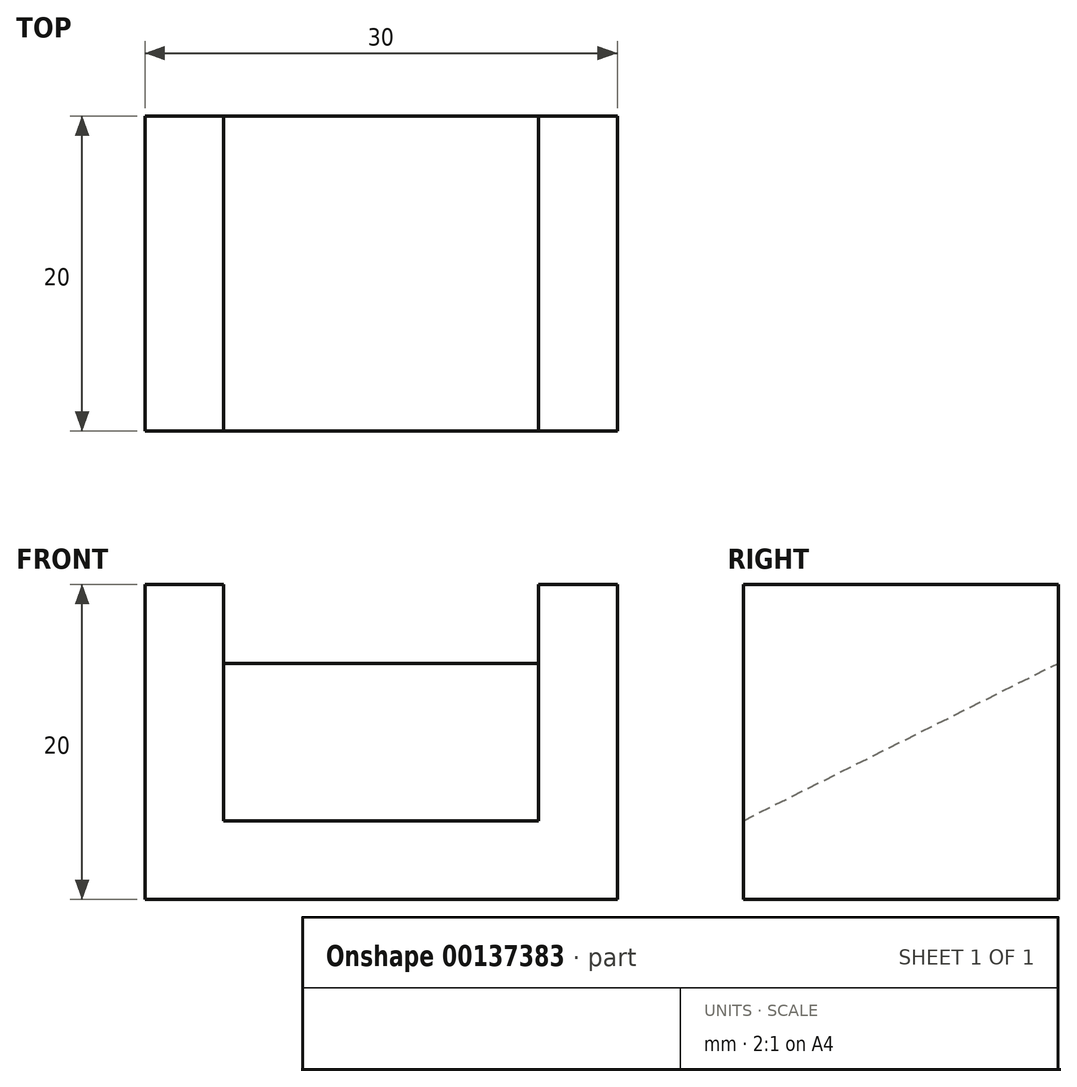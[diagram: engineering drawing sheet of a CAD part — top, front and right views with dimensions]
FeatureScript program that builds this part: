
annotation { "Feature Type Name" : "Feature", "Feature Type Description" : "" }
export const myFeature = defineFeature(function(context is Context, id is Id, definition is map)
    precondition{}
    {
        {
            var Q0;
            Q0=qCreatedBy(makeId("Front.planeOp"),FACE);
            var sketch = newSketch(context, id + "F0", { "sketchPlane" : qUnion([Q0])});
            skLineSegment(sketch, "E0.bottom", {"start": v(-15, 0) * mm, "end": v(15, 0) * mm});
            skLineSegment(sketch, "E0.top", {"start": v(-15, 20) * mm, "end": v(15, 20) * mm});
            skLineSegment(sketch, "E0.left", {"start": v(-15, 0) * mm, "end": v(-15, 20) * mm});
            skLineSegment(sketch, "E0.right", {"start": v(15, 0) * mm, "end": v(15, 20) * mm});
            skSolve(sketch);
        }
        {
            var Q0;
            Q0=qSketchRegion(id+"F0",true);
            extrude(context, id + "F1", {"entities" : qUnion([Q0]), "endBound" : BoundingType.SYMMETRIC, "depth" : 20 * mm});
        }
        {
            var Q0;
            Q0=qCreatedBy(makeId("Right.planeOp"),FACE);
            var sketch = newSketch(context, id + "F2", { "sketchPlane" : qUnion([Q0])});
            skLineSegment(sketch, "E1", {"start": v(10, 15) * mm, "end": v(10, 20) * mm});
            skLineSegment(sketch, "E2", {"start": v(10, 20) * mm, "end": v(-10, 20) * mm});
            skLineSegment(sketch, "E3", {"start": v(-10, 20) * mm, "end": v(-10, 5) * mm});
            skLineSegment(sketch, "E4", {"start": v(-10, 5) * mm, "end": v(10, 15) * mm});
            skSolve(sketch);
        }
        {
            var Q0;
            Q0=qSketchRegion(id+"F2",true);
            extrude(context, id + "F3", {"entities" : qUnion([Q0]), "operationType" : NewBodyOperationType.REMOVE, "endBound" : BoundingType.SYMMETRIC, "depth" : 20 * mm});
        }
    });
